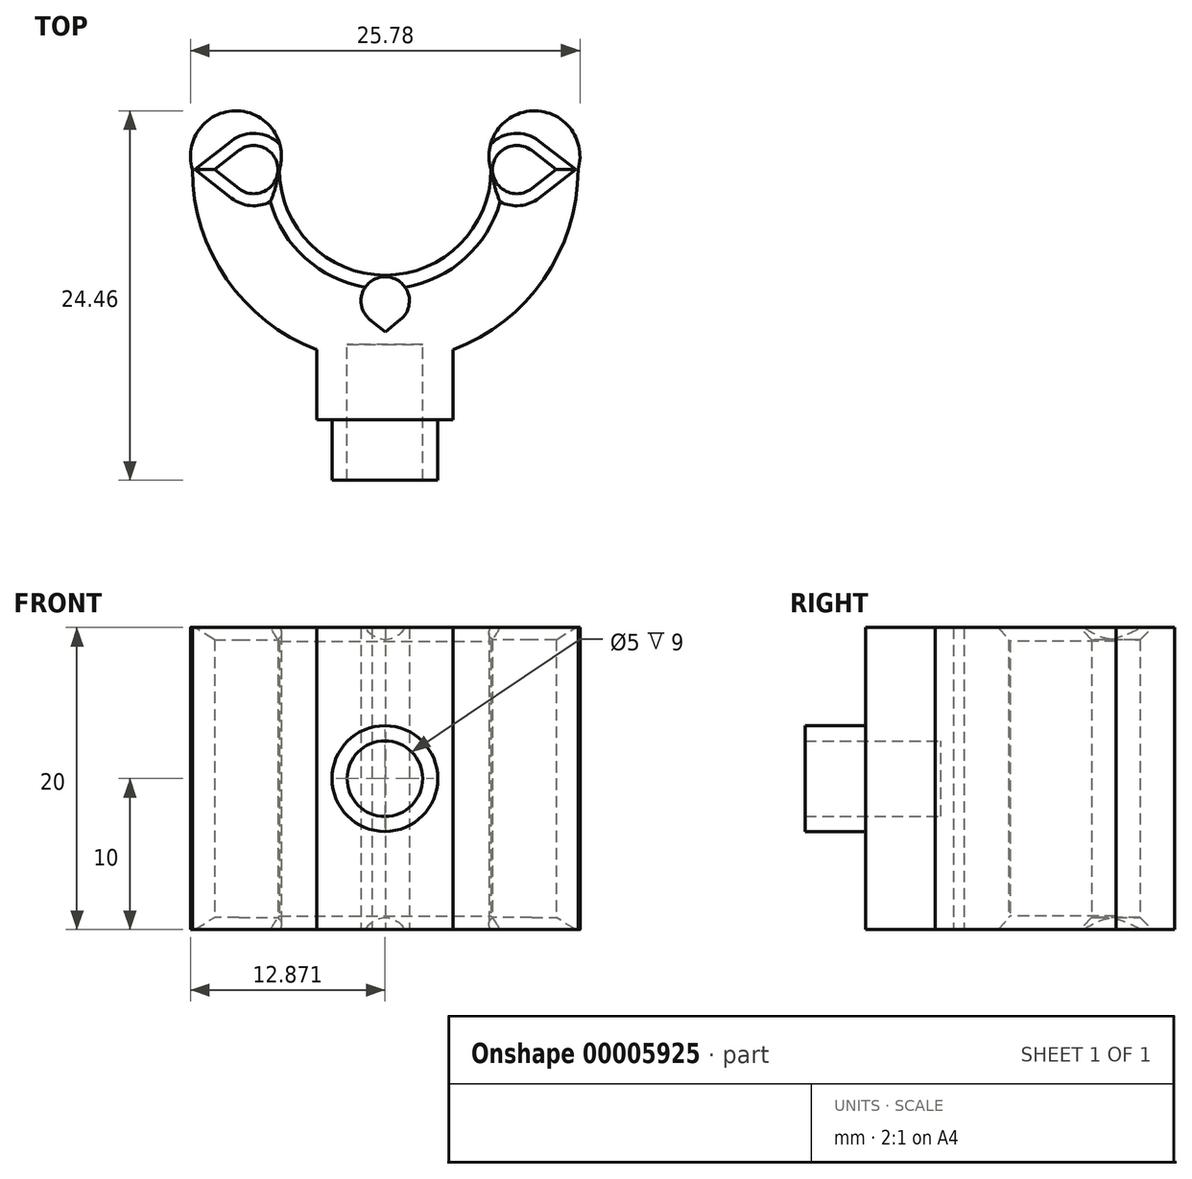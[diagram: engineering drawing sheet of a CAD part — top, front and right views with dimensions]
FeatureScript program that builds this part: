
annotation { "Feature Type Name" : "Feature", "Feature Type Description" : "" }
export const myFeature = defineFeature(function(context is Context, id is Id, definition is map)
    precondition{}
    {
        {
            var Q0;
            Q0=qCreatedBy(makeId("Top.planeOp"),FACE);
            var sketch = newSketch(context, id + "F0", { "sketchPlane" : qUnion([Q0])});
            skArc(sketch, "E0", {"start": v(-14, 0) * mm, "mid": v(-7, -7) * mm, "end": v(0, 0) * mm});
            skLineSegment(sketch, "E1", {"start": v(-7, 4.35) * mm, "end": v(-7, -12.6) * mm, "construction": true});
            skCircle(sketch, "E2.0.MirrorC", {"center": v(1.7, 0) * mm, "radius": 1.6 * mm});
            skCircle(sketch, "E3", {"center": v(-7, -8.7) * mm, "radius": 1.6 * mm});
            skArc(sketch, "E4", {"start": v(-15.7, 0) * mm, "mid": v(-7, -8.7) * mm, "end": v(1.7, 0) * mm, "construction": true});
            skLineSegment(sketch, "E5", {"start": v(-11.52, -11.93) * mm, "end": v(-11.52, -16.58) * mm});
            skLineSegment(sketch, "E6", {"start": v(-11.52, -16.58) * mm, "end": v(-2.52, -16.58) * mm});
            skLineSegment(sketch, "E7", {"start": v(-2.52, -16.58) * mm, "end": v(-2.52, -11.95) * mm});
            skLineSegment(sketch, "E8", {"start": v(-7, -12.6) * mm, "end": v(-7, -16.58) * mm, "construction": true});
            skLineSegment(sketch, "E9", {"start": v(16.16, 11.08) * mm, "end": v(16.16, -23.86) * mm, "construction": true});
            skLineSegment(sketch, "E10", {"start": v(-34.08, 12.01) * mm, "end": v(-34.08, -22.9) * mm, "construction": true});
            skLineSegment(sketch, "E11", {"start": v(-27.1, 19.77) * mm, "end": v(15.94, 19.77) * mm, "construction": true});
            skLineSegment(sketch, "E12", {"start": v(-61.03, 67.77) * mm, "end": v(-39.24, 67.77) * mm, "construction": true});
            skLineSegment(sketch, "E13", {"start": v(-8.15, -9.81) * mm, "end": v(-7, -10.76) * mm});
            skLineSegment(sketch, "E14", {"start": v(-7, -10.76) * mm, "end": v(-5.83, -9.81) * mm});
            skPoint(sketch, "E15.center.orphan", {"position": v(2.25, 0) * mm});
            skArc(sketch, "E16.0", {"start": v(-19.76, 0) * mm, "mid": v(-7, -12.76) * mm, "end": v(5.76, 0) * mm});
            skPoint(sketch, "E17.orphan", {"position": v(-2.52, -10.6) * mm});
            skPoint(sketch, "E18.orphan", {"position": v(-11.52, -10.58) * mm});
            skLineSegment(sketch, "E19", {"start": v(2.68, 1.26) * mm, "end": v(4.3, 0) * mm});
            skLineSegment(sketch, "E20", {"start": v(4.3, 0) * mm, "end": v(2.68, -1.26) * mm});
            skLineSegment(sketch, "E21.0.MirrorCS", {"start": v(-18.3, 0) * mm, "end": v(-16.68, -1.26) * mm});
            skLineSegment(sketch, "E21.1.MirrorCS", {"start": v(-16.68, 1.26) * mm, "end": v(-18.3, 0) * mm});
            skCircle(sketch, "E21.3.MirrorC", {"center": v(-15.7, 0) * mm, "radius": 1.6 * mm});
            skPoint(sketch, "E21.4.MirrorP", {"position": v(-16.25, 0) * mm});
            skArc(sketch, "E22", {"start": v(5.76, 0) * mm, "mid": v(2.88, 3.88) * mm, "end": v(0, 0) * mm});
            skArc(sketch, "E23.0.MirrorCS", {"start": v(-19.76, 0) * mm, "mid": v(-19.36, 2.57) * mm, "end": v(-17.1, 3.88) * mm});
            skArc(sketch, "E24", {"start": v(-17.1, 3.88) * mm, "mid": v(-14.53, 2.76) * mm, "end": v(-14, 0) * mm});
            skArc(sketch, "E25.1.MirrorCS", {"start": v(3.1, 3.88) * mm, "mid": v(0.53, 2.76) * mm, "end": v(0, 0) * mm});
            skArc(sketch, "E25.2.MirrorCS", {"start": v(5.76, 0) * mm, "mid": v(5.36, 2.57) * mm, "end": v(3.1, 3.88) * mm});
            skPoint(sketch, "E26", {"position": v(-17.1, 3.88) * mm});
            skPoint(sketch, "E27", {"position": v(3.1, 3.88) * mm});
            skSolve(sketch);
        }
        {
            var Q0;
            {var subQ1=sQuery(id+"F0.wireOp",EDGE,"E0");var subQ8=sQuery(id+"F0.wireOp",EDGE,"ecafd66c-8874-4360-98e2-d50b3bd03263");var subQ11=makeQuery(id+"F0.imprint","INTERSECT",VERTEX,{"derivedFrom":[subQ1,subQ8]});Q0=makeQuery(id+"F0.imprint","IMPRINT",FACE,{"disambiguationData":[TD([[makeQuery(id+"F0.imprint","IMPRINT",EDGE,{"disambiguationData":[TD([[subQ11,-1.0]])],"derivedFrom":subQ1}),-1.0]])]});}
            var Q1;
            {var subQ1=sQuery(id+"F0.wireOp",EDGE,"E5");Q1=makeQuery(id+"F0.imprint","IMPRINT",FACE,{"disambiguationData":[TD([[makeQuery(id+"F0.imprint","IMPRINT",EDGE,{"derivedFrom":subQ1}),1.0]])]});}
            extrude(context, id + "F1", {"entities" : qUnion([Q0, Q1]), "depth" : 20 * mm});
        }
        {
            var Q0;
            Q0=makeQuery(id+"F1.opExtrude","SWEPT_FACE",FACE,{"disambiguationData":[OSD([sQuery(id+"F0.wireOp",EDGE,"E6")])]});
            var sketch = newSketch(context, id + "F2", { "sketchPlane" : qUnion([Q0])});
            skLineSegment(sketch, "E28", {"start": v(-11.52, 10) * mm, "end": v(-2.52, 10) * mm, "construction": true});
            skLineSegment(sketch, "E29", {"start": v(-7.02, 20) * mm, "end": v(-7.02, 0) * mm, "construction": true});
            skCircle(sketch, "E30", {"center": v(-7.02, 10) * mm, "radius": 2.5 * mm});
            skCircle(sketch, "E31.0", {"center": v(-7.02, 10) * mm, "radius": 3.5 * mm});
            skSolve(sketch);
        }
        {
            var Q0;
            Q0=makeQuery(id+"F2.imprint","IMPRINT",FACE,{"disambiguationData":[TD([[makeQuery(id+"F2.imprint","IMPRINT",EDGE,{"derivedFrom":sQuery(id+"F2.wireOp",EDGE,"E30")}),-1.0]])]});
            extrude(context, id + "F3", {"entities" : qUnion([Q0]), "operationType" : NewBodyOperationType.ADD, "depth" : 4 * mm});
        }
        {
            var Q0;
            Q0=makeQuery(id+"F3.boolean.opBoolean","SPLIT",FACE,{"disambiguationData":[TD([makeQuery(id+"F3.opExtrude","SWEPT_FACE",FACE,{"disambiguationData":[OSD([sQuery(id+"F2.wireOp",EDGE,"E30")])]})])],"derivedFrom":makeQuery(id+"F1.opExtrude","SWEPT_FACE",FACE,{"disambiguationData":[OSD([sQuery(id+"F0.wireOp",EDGE,"E6")])]})});
            extrude(context, id + "F4", {"entities" : qUnion([Q0]), "operationType" : NewBodyOperationType.REMOVE, "oppositeDirection" : true, "depth" : 5 * mm});
        }
        {
            var Q0;
            Q0=makeQuery(id+"F1.opExtrude","CAP_EDGE",EDGE,{"disambiguationData":[OSD([sQuery(id+"F0.wireOp",EDGE,"E0")])],"isStart":false});
            var Q1;
            Q1=makeQuery(id+"F1.opExtrude","CAP_EDGE",EDGE,{"disambiguationData":[OSD([sQuery(id+"F0.wireOp",EDGE,"E0")])],"isStart":true});
            chamfer(context, id + "F5", {"entities" : qUnion([Q0, Q1]), "width" : 0.9 * mm, "tangentPropagation" : true});
        }
        {
            var Q0;
            {var subQ0=makeQuery(id+"F1.opExtrude","CAP_EDGE",EDGE,{"disambiguationData":[OSD([sQuery(id+"F0.wireOp",EDGE,"E2.0.MirrorC")])],"isStart":false});Q0=qUnion([subQ0,subQ0]);}
            var Q1;
            {var subQ0=makeQuery(id+"F1.opExtrude","CAP_EDGE",EDGE,{"disambiguationData":[OSD([sQuery(id+"F0.wireOp",EDGE,"E21.3.MirrorC")])],"isStart":false});Q1=qUnion([subQ0,subQ0]);}
            var Q2;
            {var subQ0=makeQuery(id+"F1.opExtrude","CAP_EDGE",EDGE,{"disambiguationData":[OSD([sQuery(id+"F0.wireOp",EDGE,"E2.0.MirrorC")])],"isStart":true});Q2=qUnion([subQ0,subQ0]);}
            var Q3;
            {var subQ0=makeQuery(id+"F1.opExtrude","CAP_EDGE",EDGE,{"disambiguationData":[OSD([sQuery(id+"F0.wireOp",EDGE,"E21.3.MirrorC")])],"isStart":true});Q3=qUnion([subQ0,subQ0]);}
            chamfer(context, id + "F6", {"entities" : qUnion([Q0, Q1, Q2, Q3]), "width" : 0.8 * mm, "tangentPropagation" : true});
        }
    });
